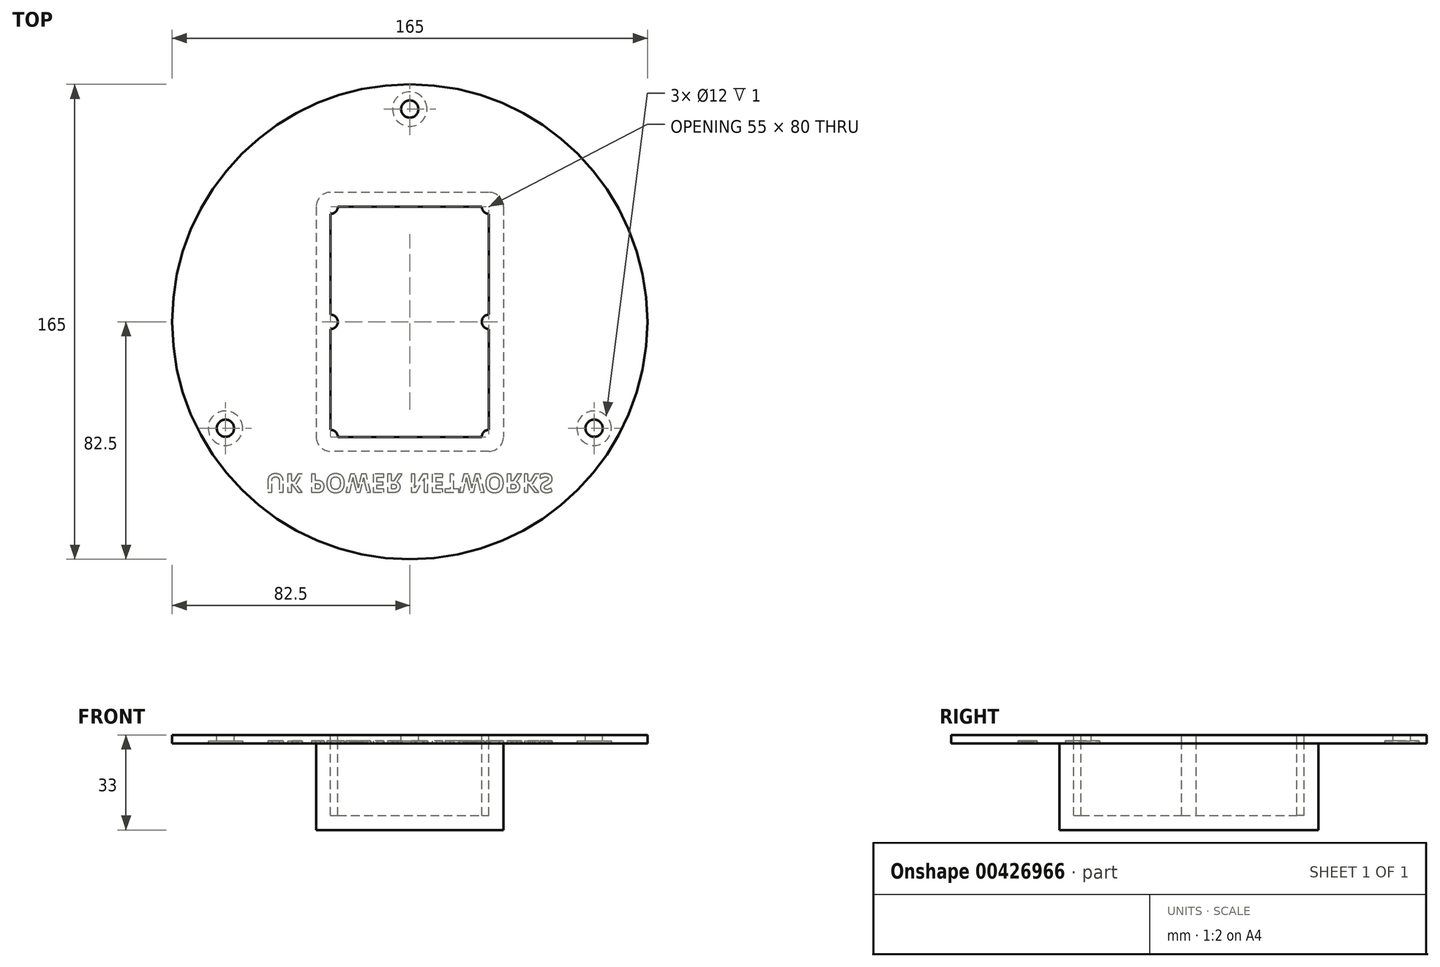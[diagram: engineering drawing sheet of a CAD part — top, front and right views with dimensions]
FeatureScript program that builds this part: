
annotation { "Feature Type Name" : "Feature", "Feature Type Description" : "" }
export const myFeature = defineFeature(function(context is Context, id is Id, definition is map)
    precondition{}
    {
        {
            var Q0;
            Q0=qCreatedBy(makeId("Top.planeOp"),FACE);
            var sketch = newSketch(context, id + "F0", { "sketchPlane" : qUnion([Q0])});
            skCircle(sketch, "E0", {"center": v(0, 0) * mm, "radius": 82.5 * mm});
            skSolve(sketch);
        }
        {
            var Q0;
            Q0 = qSketchRegion(id + "F0", true);
            extrude(context, id + "F1", {"entities" : qUnion([Q0]), "depth" : 3 * mm, "offsetDistance" : 25 * mm});
        }
        {
            var Q0;
            Q0=makeQuery(id+"F1.opExtrude","CAP_FACE",FACE,{"disambiguationData":[OSD([sQuery(id+"F0.wireOp",EDGE,"E0")])],"isStart":false});
            var sketch = newSketch(context, id + "F2", { "sketchPlane" : qUnion([Q0])});
            skLineSegment(sketch, "E1.bottom", {"start": v(27.5, 40) * mm, "end": v(-27.5, 40) * mm});
            skLineSegment(sketch, "E1.top", {"start": v(27.5, -40) * mm, "end": v(-27.5, -40) * mm});
            skLineSegment(sketch, "E1.left", {"start": v(27.5, 40) * mm, "end": v(27.5, -40) * mm});
            skLineSegment(sketch, "E1.right", {"start": v(-27.5, 40) * mm, "end": v(-27.5, -40) * mm});
            skPoint(sketch, "E1.middle", {"position": v(0, 0) * mm});
            skPoint(sketch, "E2.visualSharp", {"position": v(-27.5, 40) * mm});
            skPoint(sketch, "E3.visualSharp", {"position": v(27.5, 40) * mm});
            skPoint(sketch, "E4.visualSharp", {"position": v(27.5, -40) * mm});
            skPoint(sketch, "E5.visualSharp", {"position": v(-27.5, -40) * mm});
            skCircle(sketch, "E6", {"center": v(-27.5, 40) * mm, "radius": 2.5 * mm});
            skCircle(sketch, "E7", {"center": v(27.5, 40) * mm, "radius": 2.5 * mm});
            skCircle(sketch, "E8", {"center": v(27.5, 0) * mm, "radius": 2.5 * mm});
            skCircle(sketch, "E9", {"center": v(27.5, -40) * mm, "radius": 2.5 * mm});
            skCircle(sketch, "E10", {"center": v(-27.5, -40) * mm, "radius": 2.5 * mm});
            skCircle(sketch, "E11", {"center": v(-27.5, 0) * mm, "radius": 2.5 * mm});
            skSolve(sketch);
        }
        {
            var Q0;
            Q0=makeQuery(id+"F1.opExtrude","CAP_FACE",FACE,{"disambiguationData":[OSD([sQuery(id+"F0.wireOp",EDGE,"E0")])],"isStart":false});
            var sketch = newSketch(context, id + "F3", { "sketchPlane" : qUnion([Q0])});
            skCircle(sketch, "E12", {"center": v(0, 0) * mm, "radius": 73.9 * mm});
            skCircle(sketch, "E13", {"center": v(0, 73.9) * mm, "radius": 3 * mm});
            skCircle(sketch, "E14", {"center": v(64, -36.95) * mm, "radius": 3 * mm});
            skCircle(sketch, "E15", {"center": v(-64, -36.95) * mm, "radius": 3 * mm});
            skSolve(sketch);
        }
        {
            var Q0;
            {var subQ0=sQuery(id+"F3.wireOp",EDGE,"E13");var subQ1=sQuery(id+"F3.wireOp",EDGE,"E12");var subQ2=makeQuery(id+"F3.imprint","INTERSECT",VERTEX,{"disambiguationData":[OD(0.0)],"derivedFrom":[subQ1,subQ0]});Q0=makeQuery(id+"F3.imprint","IMPRINT",FACE,{"disambiguationData":[TD([[makeQuery(id+"F3.imprint","IMPRINT",EDGE,{"disambiguationData":[TD([[subQ2,1.0]])],"derivedFrom":subQ1}),1.0]])]});}
            var Q1;
            {var subQ0=sQuery(id+"F3.wireOp",EDGE,"E13");var subQ1=sQuery(id+"F3.wireOp",EDGE,"E12");var subQ2=makeQuery(id+"F3.imprint","INTERSECT",VERTEX,{"disambiguationData":[OD(0.0)],"derivedFrom":[subQ1,subQ0]});Q1=makeQuery(id+"F3.imprint","IMPRINT",FACE,{"disambiguationData":[TD([[makeQuery(id+"F3.imprint","IMPRINT",EDGE,{"disambiguationData":[TD([[subQ2,1.0]])],"derivedFrom":subQ1}),-1.0]])]});}
            var Q2;
            {var subQ0=sQuery(id+"F3.wireOp",EDGE,"E15");var subQ1=sQuery(id+"F3.wireOp",EDGE,"E12");var subQ2=makeQuery(id+"F3.imprint","INTERSECT",VERTEX,{"disambiguationData":[OD(0.0)],"derivedFrom":[subQ1,subQ0]});Q2=makeQuery(id+"F3.imprint","IMPRINT",FACE,{"disambiguationData":[TD([[makeQuery(id+"F3.imprint","IMPRINT",EDGE,{"disambiguationData":[TD([[subQ2,-1.0]])],"derivedFrom":subQ1}),-1.0]])]});}
            var Q3;
            {var subQ0=sQuery(id+"F3.wireOp",EDGE,"E15");var subQ1=sQuery(id+"F3.wireOp",EDGE,"E12");var subQ2=makeQuery(id+"F3.imprint","INTERSECT",VERTEX,{"disambiguationData":[OD(0.0)],"derivedFrom":[subQ1,subQ0]});Q3=makeQuery(id+"F3.imprint","IMPRINT",FACE,{"disambiguationData":[TD([[makeQuery(id+"F3.imprint","IMPRINT",EDGE,{"disambiguationData":[TD([[subQ2,-1.0]])],"derivedFrom":subQ1}),1.0]])]});}
            var Q4;
            {var subQ0=sQuery(id+"F3.wireOp",EDGE,"E14");var subQ1=sQuery(id+"F3.wireOp",EDGE,"E12");var subQ2=makeQuery(id+"F3.imprint","INTERSECT",VERTEX,{"disambiguationData":[OD(0.0)],"derivedFrom":[subQ1,subQ0]});Q4=makeQuery(id+"F3.imprint","IMPRINT",FACE,{"disambiguationData":[TD([[makeQuery(id+"F3.imprint","IMPRINT",EDGE,{"disambiguationData":[TD([[subQ2,-1.0]])],"derivedFrom":subQ1}),-1.0]])]});}
            var Q5;
            {var subQ0=sQuery(id+"F3.wireOp",EDGE,"E14");var subQ1=sQuery(id+"F3.wireOp",EDGE,"E12");var subQ2=makeQuery(id+"F3.imprint","INTERSECT",VERTEX,{"disambiguationData":[OD(0.0)],"derivedFrom":[subQ1,subQ0]});Q5=makeQuery(id+"F3.imprint","IMPRINT",FACE,{"disambiguationData":[TD([[makeQuery(id+"F3.imprint","IMPRINT",EDGE,{"disambiguationData":[TD([[subQ2,-1.0]])],"derivedFrom":subQ1}),1.0]])]});}
            extrude(context, id + "F4", {"entities" : qUnion([Q0, Q1, Q2, Q3, Q4, Q5]), "operationType" : NewBodyOperationType.REMOVE, "oppositeDirection" : true, "depth" : 25 * mm, "offsetDistance" : 25 * mm});
        }
        {
            var Q0;
            {var subQ6=sQuery(id+"F2.wireOp",EDGE,"E1.bottom");var subQ15=sQuery(id+"F2.wireOp",EDGE,"E7");var subQ16=makeQuery(id+"F2.imprint","INTERSECT",VERTEX,{"derivedFrom":[subQ6,subQ15]});Q0=makeQuery(id+"F2.imprint","IMPRINT",FACE,{"disambiguationData":[TD([[makeQuery(id+"F2.imprint","IMPRINT",EDGE,{"disambiguationData":[TD([[subQ16,-1.0]])],"derivedFrom":subQ6}),1.0]])]});}
            extrude(context, id + "F5", {"entities" : qUnion([Q0]), "operationType" : NewBodyOperationType.REMOVE, "endBound" : BoundingType.UP_TO_NEXT, "oppositeDirection" : true, "depth" : 25 * mm, "offsetDistance" : 25 * mm});
        }
        {
            var Q0;
            Q0=makeQuery(id+"F1.opExtrude","CAP_FACE",FACE,{"disambiguationData":[OSD([sQuery(id+"F0.wireOp",EDGE,"E0")])],"isStart":true});
            var sketch = newSketch(context, id + "F6", { "sketchPlane" : qUnion([Q0])});
            skLineSegment(sketch, "E16.bottom", {"start": v(27.5, -45) * mm, "end": v(-27.5, -45) * mm});
            skLineSegment(sketch, "E16.top", {"start": v(27.5, 45) * mm, "end": v(-27.5, 45) * mm});
            skLineSegment(sketch, "E16.left", {"start": v(32.5, -40) * mm, "end": v(32.5, 40) * mm});
            skLineSegment(sketch, "E16.right", {"start": v(-32.5, -40) * mm, "end": v(-32.5, 40) * mm});
            skPoint(sketch, "E16.middle", {"position": v(0, 0) * mm});
            skPoint(sketch, "E17.visualSharp", {"position": v(-32.5, 45) * mm});
            skArc(sketch, "E17.filletArc", {"start": v(-27.5, 45) * mm, "mid": v(-31.04, 43.54) * mm, "end": v(-32.5, 40) * mm});
            skPoint(sketch, "E18.visualSharp", {"position": v(32.5, 45) * mm});
            skArc(sketch, "E18.filletArc", {"start": v(32.5, 40) * mm, "mid": v(31.04, 43.54) * mm, "end": v(27.5, 45) * mm});
            skPoint(sketch, "E19.visualSharp", {"position": v(32.5, -45) * mm});
            skArc(sketch, "E19.filletArc", {"start": v(27.5, -45) * mm, "mid": v(31.04, -43.54) * mm, "end": v(32.5, -40) * mm});
            skPoint(sketch, "E20.visualSharp", {"position": v(-32.5, -45) * mm});
            skArc(sketch, "E20.filletArc", {"start": v(-32.5, -40) * mm, "mid": v(-31.04, -43.54) * mm, "end": v(-27.5, -45) * mm});
            skSolve(sketch);
        }
        {
            var Q0;
            Q0 = qSketchRegion(id + "F6", true);
            extrude(context, id + "F7", {"entities" : qUnion([Q0]), "depth" : 30 * mm, "offsetDistance" : 25 * mm});
        }
        {
            var Q0;
            Q0=makeQuery(id+"F7.opExtrude","CAP_FACE",FACE,{"disambiguationData":[OSD([sQuery(id+"F6.wireOp",EDGE,"E16.bottom"),sQuery(id+"F6.wireOp",EDGE,"E16.top"),sQuery(id+"F6.wireOp",EDGE,"E16.left"),sQuery(id+"F6.wireOp",EDGE,"E16.right"),sQuery(id+"F6.wireOp",EDGE,"E17.filletArc"),sQuery(id+"F6.wireOp",EDGE,"E18.filletArc"),sQuery(id+"F6.wireOp",EDGE,"E19.filletArc"),sQuery(id+"F6.wireOp",EDGE,"E20.filletArc")])],"isStart":true});
            var sketch = newSketch(context, id + "F8", { "sketchPlane" : qUnion([Q0])});
            skArc(sketch, "E21.0", {"start": v(25, -40) * mm, "mid": v(25.73, -38.23) * mm, "end": v(27.5, -37.5) * mm});
            skLineSegment(sketch, "E21.1", {"start": v(-25, 40) * mm, "end": v(25, 40) * mm});
            skArc(sketch, "E21.2", {"start": v(27.5, 37.5) * mm, "mid": v(25.73, 38.23) * mm, "end": v(25, 40) * mm});
            skLineSegment(sketch, "E21.3", {"start": v(27.5, 2.5) * mm, "end": v(27.5, 37.5) * mm});
            skArc(sketch, "E21.4", {"start": v(27.5, -2.5) * mm, "mid": v(25, 0) * mm, "end": v(27.5, 2.5) * mm});
            skArc(sketch, "E21.5", {"start": v(-25, 40) * mm, "mid": v(-25.73, 38.23) * mm, "end": v(-27.5, 37.5) * mm});
            skLineSegment(sketch, "E21.6", {"start": v(27.5, -37.5) * mm, "end": v(27.5, -2.5) * mm});
            skLineSegment(sketch, "E21.7", {"start": v(-27.5, 2.5) * mm, "end": v(-27.5, 37.5) * mm});
            skArc(sketch, "E21.8", {"start": v(-27.5, 2.5) * mm, "mid": v(-25, 0) * mm, "end": v(-27.5, -2.5) * mm});
            skLineSegment(sketch, "E21.9", {"start": v(-27.5, -37.5) * mm, "end": v(-27.5, -2.5) * mm});
            skArc(sketch, "E21.10", {"start": v(-27.5, -37.5) * mm, "mid": v(-25.73, -38.23) * mm, "end": v(-25, -40) * mm});
            skLineSegment(sketch, "E21.11", {"start": v(-25, -40) * mm, "end": v(25, -40) * mm});
            skSolve(sketch);
        }
        {
            var Q0;
            Q0 = qSketchRegion(id + "F8", true);
            extrude(context, id + "F9", {"entities" : qUnion([Q0]), "operationType" : NewBodyOperationType.REMOVE, "oppositeDirection" : true, "depth" : 25 * mm, "offsetDistance" : 25 * mm});
        }
        {
            var Q0;
            Q0=makeQuery(id+"F1.opExtrude","CAP_FACE",FACE,{"disambiguationData":[OSD([sQuery(id+"F0.wireOp",EDGE,"E0")])],"isStart":true});
            var sketch = newSketch(context, id + "F10", { "sketchPlane" : qUnion([Q0])});
            skCircle(sketch, "E22.0", {"center": v(-64, 36.95) * mm, "radius": 6 * mm});
            skCircle(sketch, "E23.0", {"center": v(64, 36.95) * mm, "radius": 6 * mm});
            skCircle(sketch, "E24.0", {"center": v(0, -73.9) * mm, "radius": 6 * mm});
            skSolve(sketch);
        }
        {
            var Q0;
            Q0 = qSketchRegion(id + "F10", true);
            extrude(context, id + "F11", {"entities" : qUnion([Q0]), "operationType" : NewBodyOperationType.REMOVE, "oppositeDirection" : true, "depth" : 1 * mm, "offsetDistance" : 25 * mm});
        }
        {
            var Q0;
            Q0=makeQuery(id+"F1.opExtrude","CAP_FACE",FACE,{"disambiguationData":[OSD([sQuery(id+"F0.wireOp",EDGE,"E0")])],"isStart":true});
            var sketch = newSketch(context, id + "F12", { "sketchPlane" : qUnion([Q0])});
            skText(sketch, "E25", { "text": "UK POWER NETWORKS", "fontName": "OpenSans-Bold.ttf"});
            const initialGuessF12  = {"E25": [-0.05, 0.05283, 1, 0, 0.00645]};
            skSetInitialGuess(sketch, initialGuessF12);
            skSolve(sketch);
        }
        {
            var Q0;
            Q0 = qSketchRegion(id + "F12", true);
            extrude(context, id + "F13", {"entities" : qUnion([Q0]), "operationType" : NewBodyOperationType.REMOVE, "oppositeDirection" : true, "depth" : 1 * mm, "offsetDistance" : 25 * mm});
        }
    });
